# Revit family: Toilet-Floor_Mount-KOHLER-Tresham-K-3950
name_source: partatom
category: Plumbing Fixtures
revit_build: Autodesk Revit 2015 (Build: 20140606_1530(x64)
units: mm (PartAtom-declared; Revit-internal decimal feet)

## types (12) — shared parameters
ADA Compliant = Yes
Assembly Code = D2010100
CW Connection = Yes
Cold Water Inlet = Cold Water Inlet
Date Modified = 01/02/2019
Default Elevation = 0"
Flow Rate = 0 GPM
Flush Rate = 1.28 GPF
HW Connection = No
Height = 31 1/4"
Hot Water Inlet = Hot Water Inlet
Length = 29 3/16"
Manufacturer = KOHLER Co.
MasterFormat 1995 = 15410
MasterFormat 2004 = 22.41.13
Material = Vitreous China
Pressure = 0.00 psi
Product Documentation Link = http://www.us.kohler.com
Product Name = Tresham
Product Page URL = http://www.us.kohler.com
Rough-In = 12"
Seat Included = No
URL = https://www.us.kohler.com
Vent Connection = No
Waste Connection = Yes
Waste Water Outlet = Waste Water Outlet
Width = 16 5/8"

## per-type parameters (varying)
| type | Description | Finish | Left-hand trip lever | Model | Right-hand trip lever | Type |
| Left-hand trip lever, 0-White | Comfort Height two-piece elongated 1.28 gpf toilet with AquaPiston flushing technology and left-hand trip lever, seat not included | Kohler-Vitreous_China-0-White | Yes | K-3950-0 | No | 1 |
| Left-hand trip lever, 96-Biscuit | Comfort Height two-piece elongated 1.28 gpf toilet with AquaPiston flushing technology and left-hand trip lever, seat not included | Kohler-Vitreous_China-96-Biscuit | Yes | K-3950-96 | No | 2 |
| Left-hand trip lever, 47-Almond | Comfort Height two-piece elongated 1.28 gpf toilet with AquaPiston flushing technology and left-hand trip lever, seat not included | Kohler-Vitreous_China-47-Almond | Yes | K-3950-47 | No | 3 |
| Left-hand trip lever, 7-Black Black | Comfort Height two-piece elongated 1.28 gpf toilet with AquaPiston flushing technology and left-hand trip lever, seat not included | Kohler-Vitreous_China-7-Black_Black | Yes | K-3950-7 | No | 9 |
| Right-hand trip lever, 0-White | Comfort Height two-piece elongated 1.28 gpf toilet with right-hand trip lever, seat not included | Kohler-Vitreous_China-0-White | No | K-3950-RA-0 | Yes | 10 |
| Right-hand trip lever, 96-Biscuit | Comfort Height two-piece elongated 1.28 gpf toilet with right-hand trip lever, seat not included | Kohler-Vitreous_China-96-Biscuit | No | K-3950-RA-96 | Yes | 11 |
| Right-hand trip lever, 47-Almond | Comfort Height two-piece elongated 1.28 gpf toilet with right-hand trip lever, seat not included | Kohler-Vitreous_China-47-Almond | No | K-3950-RA-47 | Yes | 12 |
| Left-hand trip lever, NY-Dune | Comfort Height two-piece elongated 1.28 gpf toilet with AquaPiston flushing technology and left-hand trip lever, seat not included | Kohler-Vitreous_China-NY-Dune | Yes | K-3950-NY | No | 4 |
| Left-hand trip lever, 95-Ice Grey | Comfort Height two-piece elongated 1.28 gpf toilet with AquaPiston flushing technology and left-hand trip lever, seat not included | Kohler-Vitreous_China-95-Ice_Grey | Yes | K-3950-95 | No | 5 |
| Left-hand trip lever, G9-Sandbar | Comfort Height two-piece elongated 1.28 gpf toilet with AquaPiston flushing technology and left-hand trip lever, seat not included | Kohler-Vitreous_China-G9-Sandbar | Yes | K-3950-G9 | No | 6 |
| Left-hand trip lever, K4-Cashmere | Comfort Height two-piece elongated 1.28 gpf toilet with AquaPiston flushing technology and left-hand trip lever, seat not included | Kohler-Vitreous_China-K4-Cashmere | Yes | K-3950-K4 | No | 7 |
| Left-hand trip lever, 58-Thunder Grey | Comfort Height two-piece elongated 1.28 gpf toilet with AquaPiston flushing technology and left-hand trip lever, seat not included | Kohler-Vitreous_China-58-Thunder_Grey | Yes | K-3950-58 | No | 8 |

## geometry (parser evidence)
native form markers: Sweep x6
no freeform markers — native parametric forms only
